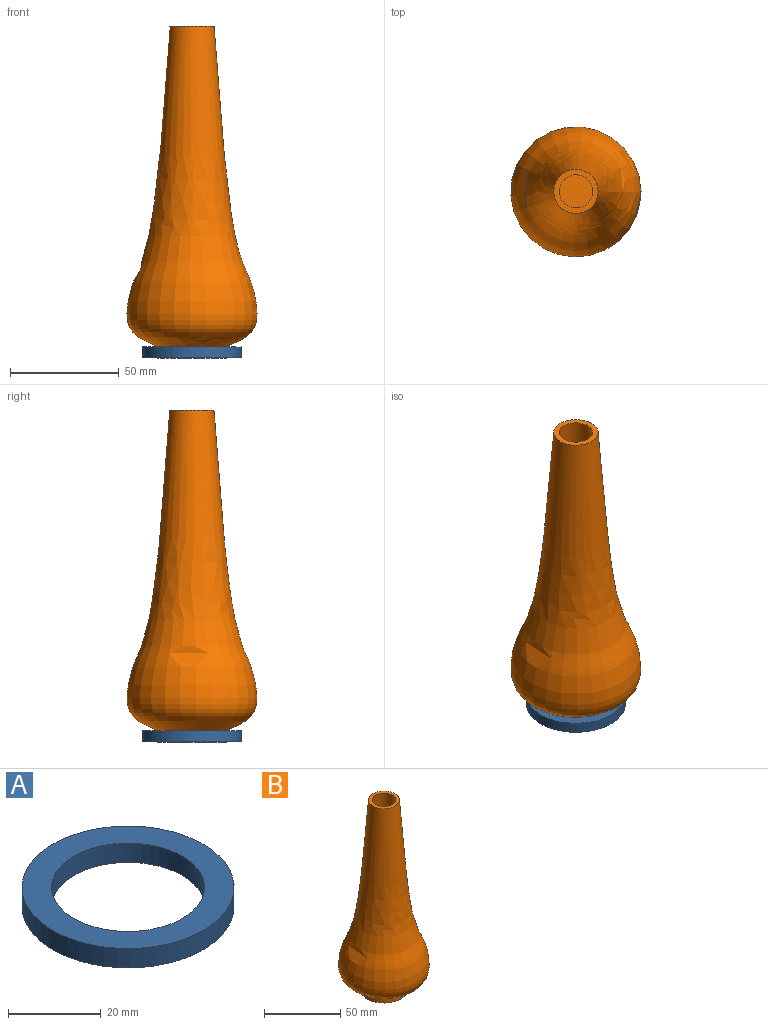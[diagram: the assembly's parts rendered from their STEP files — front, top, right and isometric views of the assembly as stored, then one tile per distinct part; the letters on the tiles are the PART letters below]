
ASSEMBLY  parts=2 mates=1
PART A: 6 faces, bbox 45.6x45.6x5.1 mm
  f0: revolved ~32.93x32.93mm, area 0mm2, adj f4,f5
  f1: revolved ~45.63x45.63mm, area 0mm2, adj f2,f5
  f2: cylinder r=22.82mm len=45.63mm, axis (0,0,1), area 728.2mm2, adj f1,f3
  f3: plane 45.63x45.63mm, normal (0,0,1), area 783.6mm2, adj f2,f4
  f4: cylinder r=16.47mm len=32.93mm, axis (0,0,1), area 525.5mm2, adj f0,f3
  f5: plane 45.63x45.63mm, normal (0,0,-1), area 783.6mm2, adj f0,f1
PART B: 7 faces, bbox 59.7x59.7x152.4 mm
  f0: plane 20.32x20.32mm, normal (0,0,1), area 142.2mm2, adj f1,f4
  f1: revolved ~147.32x59.73mm, area 18044.5mm2, adj f0,f2
  f2: cylinder r=15.88mm len=31.75mm, axis (0,0,1), area 506.7mm2, adj f1,f3
  f3: plane 31.75x31.75mm, normal (0,0,-1), area 791.7mm2, adj f2
  f4: revolved ~145.68x54.57mm, area 15297.3mm2, adj f0,f5
  f5: cylinder r=13.33mm len=26.67mm, axis (0,0,1), area 350.2mm2, adj f4,f6
  f6: plane 26.67x26.67mm, normal (0,0,1), area 558.6mm2, adj f5
PLACE A t=(0,0,9.79)mm
PLACE B at identity
MATE fastened A.f2 <-> B.f2  axis (0,0,1) through (0,0,-26.41)mm
